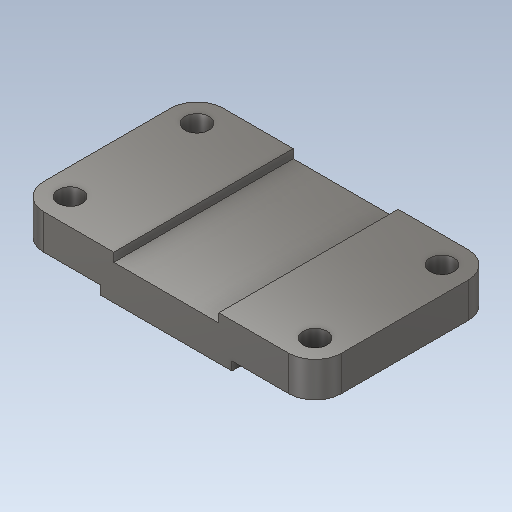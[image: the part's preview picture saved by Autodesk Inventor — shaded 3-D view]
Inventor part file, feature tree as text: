
AUTODESK INVENTOR PART (.ipt)
format: ipt  version: 2020 (Build 240168000, 168)  size: 171,520 bytes
history: native  units: mm
features: extrude x3, sketch x2, fillet x2, mirror x1
ambient origin geometry x8: Origin, YZ Plane, XZ Plane, XY Plane, X Axis, Y Axis, Z Axis, Center Point
bodies: Solid1 (feature_tree)
feature tree (8):
  extrude  "Extrusion1"  Depth=4.0mm
  sketch  "Sketch2"  dims[d2=38.0mm d3=16.0mm d4=44.0mm d5=4.0mm d6=82.0mm d7=0.0mm d8=11.0mm d9=11.0mm d10=12.0mm d11=12.0mm d12=12.0mm d13=12.0mm d14=82.0mm d15=0.0mm d16=82.0mm d17=0.0mm d18=12.0mm d19=12.0mm]
  extrude  "Extrusion2"  Depth=16.0mm
  extrude  "Extrusion3"  Depth=44.0mm
  fillet  "Fillet1"  Radius=4.0mm
  fillet  "Fillet2"  Radius=82.0mm
  mirror  "Mirror1"
  sketch  "Sketch1"  dims[d0=30.0mm d1=4.0mm]
